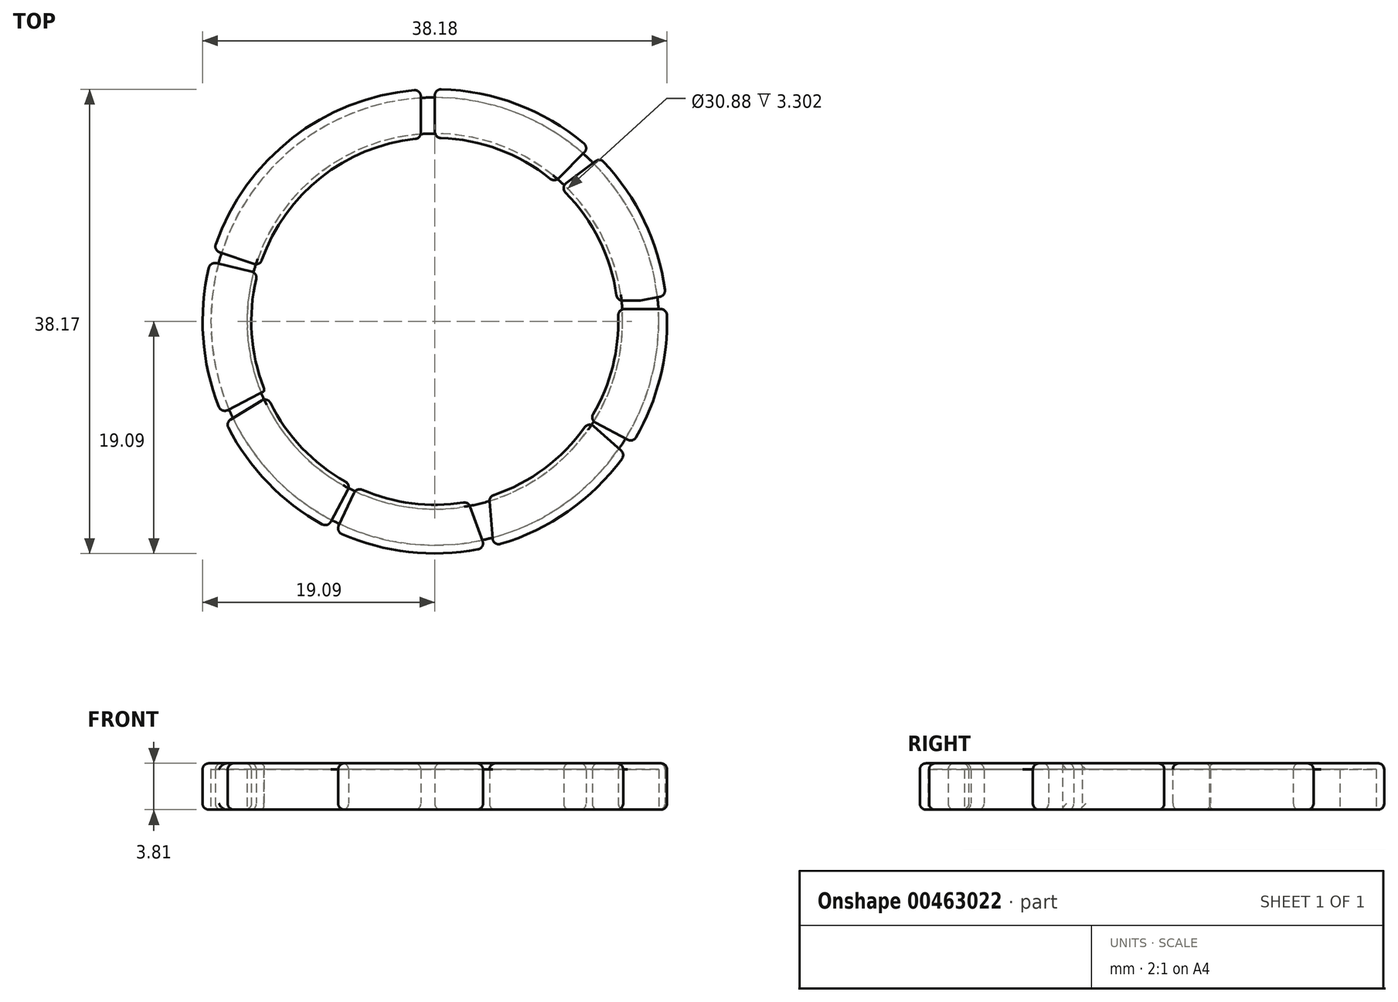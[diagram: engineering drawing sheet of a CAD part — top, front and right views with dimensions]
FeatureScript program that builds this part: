
annotation { "Feature Type Name" : "Feature", "Feature Type Description" : "" }
export const myFeature = defineFeature(function(context is Context, id is Id, definition is map)
    precondition{}
    {
        {
            var Q0;
            Q0=qCreatedBy(makeId("Top.planeOp"),FACE);
            var sketch = newSketch(context, id + "F0", { "sketchPlane" : qUnion([Q0])});
            skCircle(sketch, "E0", {"center": v(0, 0) * mm, "radius": 15.08 * mm});
            skCircle(sketch, "E1", {"center": v(0, 0) * mm, "radius": 19.09 * mm});
            skSolve(sketch);
        }
        {
            var Q0;
            Q0=makeQuery(id+"F0.imprint","IMPRINT",FACE,{"disambiguationData":[TD([[makeQuery(id+"F0.imprint","IMPRINT",EDGE,{"derivedFrom":sQuery(id+"F0.wireOp",EDGE,"E0")}),-1.0]])]});
            extrude(context, id + "F1", {"entities" : qUnion([Q0]), "depth" : 3.8 * mm});
        }
        {
            var Q0;
            Q0=qCreatedBy(makeId("Top.planeOp"),FACE);
            var sketch = newSketch(context, id + "F2", { "sketchPlane" : qUnion([Q0])});
            skLineSegment(sketch, "E2", {"start": v(-1.15, 20.08) * mm, "end": v(-1.15, 14.74) * mm});
            skLineSegment(sketch, "E3", {"start": v(-1.15, 14.74) * mm, "end": v(0, 14.74) * mm});
            skLineSegment(sketch, "E4", {"start": v(0, 14.74) * mm, "end": v(0, 20.5) * mm});
            skLineSegment(sketch, "E5", {"start": v(-1.15, 20.08) * mm, "end": v(0, 20.5) * mm});
            skLineSegment(sketch, "E6", {"start": v(9.54, 11.12) * mm, "end": v(13.13, 14.74) * mm});
            skLineSegment(sketch, "E7", {"start": v(13.13, 14.74) * mm, "end": v(14.06, 13.81) * mm});
            skLineSegment(sketch, "E8", {"start": v(14.06, 13.81) * mm, "end": v(9.54, 10.42) * mm});
            skLineSegment(sketch, "E9", {"start": v(9.54, 10.42) * mm, "end": v(9.54, 11.12) * mm});
            skLineSegment(sketch, "E10", {"start": v(-14.05, 4.45) * mm, "end": v(-18.62, 6) * mm});
            skLineSegment(sketch, "E11", {"start": v(-18.62, 6) * mm, "end": v(-18.62, 4.94) * mm});
            skLineSegment(sketch, "E12", {"start": v(-18.62, 4.94) * mm, "end": v(-14.2, 3.88) * mm});
            skLineSegment(sketch, "E13", {"start": v(-14.2, 3.88) * mm, "end": v(-14.05, 4.45) * mm});
            skLineSegment(sketch, "E14", {"start": v(-17.85, -7.72) * mm, "end": v(-14.05, -5.75) * mm});
            skLineSegment(sketch, "E15", {"start": v(-14.05, -5.75) * mm, "end": v(-13.37, -5.98) * mm});
            skLineSegment(sketch, "E16", {"start": v(-13.37, -5.98) * mm, "end": v(-17.5, -8.5) * mm});
            skLineSegment(sketch, "E17", {"start": v(-17.5, -8.5) * mm, "end": v(-17.85, -7.72) * mm});
            skLineSegment(sketch, "E18", {"start": v(-6.8, -13.21) * mm, "end": v(-8.91, -17.15) * mm});
            skLineSegment(sketch, "E19", {"start": v(-8.91, -17.15) * mm, "end": v(-8.18, -17.4) * mm});
            skLineSegment(sketch, "E20", {"start": v(-8.18, -17.4) * mm, "end": v(-6.31, -13.42) * mm});
            skLineSegment(sketch, "E21", {"start": v(2.55, -14.27) * mm, "end": v(4.38, -19.33) * mm});
            skLineSegment(sketch, "E22", {"start": v(4.38, -19.33) * mm, "end": v(4.89, -19.5) * mm});
            skLineSegment(sketch, "E23", {"start": v(4.89, -19.5) * mm, "end": v(4.38, -13.42) * mm});
            skLineSegment(sketch, "E24", {"start": v(4.38, -13.42) * mm, "end": v(2.55, -14.27) * mm});
            skLineSegment(sketch, "E25", {"start": v(12.05, -7.72) * mm, "end": v(15.85, -11.1) * mm});
            skLineSegment(sketch, "E26", {"start": v(15.85, -11.1) * mm, "end": v(16.67, -10.17) * mm});
            skLineSegment(sketch, "E27", {"start": v(16.67, -10.17) * mm, "end": v(12.05, -7.72) * mm});
            skLineSegment(sketch, "E28", {"start": v(14.16, 1.7) * mm, "end": v(16.83, 1.7) * mm});
            skLineSegment(sketch, "E29", {"start": v(16.83, 1.7) * mm, "end": v(19.72, 2.27) * mm});
            skLineSegment(sketch, "E30", {"start": v(19.72, 2.27) * mm, "end": v(19.96, 1) * mm});
            skLineSegment(sketch, "E31", {"start": v(19.96, 1) * mm, "end": v(14.16, 1) * mm});
            skLineSegment(sketch, "E32", {"start": v(14.16, 1) * mm, "end": v(14.16, 1.7) * mm});
            skLineSegment(sketch, "E33", {"start": v(-6.31, -13.42) * mm, "end": v(-6.8, -13.21) * mm});
            skSolve(sketch);
        }
        {
            var Q0;
            Q0 = qSketchRegion(id + "F2", true);
            extrude(context, id + "F3", {"entities" : qUnion([Q0]), "operationType" : NewBodyOperationType.REMOVE, "oppositeDirection" : true, "depth" : -25.4 * mm});
        }
        {
            var Q0;
            {var subQ0=sQuery(id+"F0.wireOp",EDGE,"E1");Q0=makeQuery(id+"F3.boolean.opBoolean","SPLIT",EDGE,{"disambiguationData":[TD([makeQuery(id+"F3.opExtrude","SWEPT_FACE",FACE,{"disambiguationData":[OSD([sQuery(id+"F2.wireOp",EDGE,"E4")])]})])],"derivedFrom":makeQuery(id+"F1.opExtrude","CAP_EDGE",EDGE,{"disambiguationData":[OSD([subQ0])],"isStart":false})});}
            var Q1;
            {var subQ0=sQuery(id+"F0.wireOp",EDGE,"E1");Q1=makeQuery(id+"F3.boolean.opBoolean","SPLIT",FACE,{"disambiguationData":[TD([makeQuery(id+"F3.opExtrude","SWEPT_FACE",FACE,{"disambiguationData":[OSD([sQuery(id+"F2.wireOp",EDGE,"E4")])]})])],"derivedFrom":makeQuery(id+"F1.opExtrude","SWEPT_FACE",FACE,{"disambiguationData":[OSD([subQ0])]})});}
            var Q2;
            {var subQ0=sQuery(id+"F0.wireOp",EDGE,"E0");var subQ1=sQuery(id+"F0.wireOp",EDGE,"E1");Q2=makeQuery(id+"F3.boolean.opBoolean","SPLIT",FACE,{"disambiguationData":[TD([makeQuery(id+"F3.opExtrude","SWEPT_FACE",FACE,{"disambiguationData":[OSD([sQuery(id+"F2.wireOp",EDGE,"E4")])]})])],"derivedFrom":makeQuery(id+"F1.opExtrude","CAP_FACE",FACE,{"disambiguationData":[OSD([subQ0,subQ1])],"isStart":true})});}
            var Q3;
            {var subQ0=sQuery(id+"F0.wireOp",EDGE,"E1");Q3=makeQuery(id+"F3.boolean.opBoolean","SPLIT",EDGE,{"disambiguationData":[TD([makeQuery(id+"F3.opExtrude","SWEPT_FACE",FACE,{"disambiguationData":[OSD([sQuery(id+"F2.wireOp",EDGE,"E4")])]})])],"derivedFrom":makeQuery(id+"F1.opExtrude","CAP_EDGE",EDGE,{"disambiguationData":[OSD([subQ0])],"isStart":true})});}
            var Q4;
            {var subQ0=sQuery(id+"F0.wireOp",EDGE,"E0");Q4=makeQuery(id+"F3.boolean.opBoolean","SPLIT",EDGE,{"disambiguationData":[TD([makeQuery(id+"F3.opExtrude","SWEPT_FACE",FACE,{"disambiguationData":[OSD([sQuery(id+"F2.wireOp",EDGE,"E4")])]})])],"derivedFrom":makeQuery(id+"F1.opExtrude","CAP_EDGE",EDGE,{"disambiguationData":[OSD([subQ0])],"isStart":false})});}
            var Q5;
            {var subQ0=sQuery(id+"F0.wireOp",EDGE,"E0");Q5=makeQuery(id+"F3.boolean.opBoolean","SPLIT",EDGE,{"disambiguationData":[TD([makeQuery(id+"F3.opExtrude","SWEPT_FACE",FACE,{"disambiguationData":[OSD([sQuery(id+"F2.wireOp",EDGE,"E4")])]})])],"derivedFrom":makeQuery(id+"F1.opExtrude","CAP_EDGE",EDGE,{"disambiguationData":[OSD([subQ0])],"isStart":true})});}
            var Q6;
            {var subQ1=sQuery(id+"F0.wireOp",EDGE,"E0");Q6=makeQuery(id+"F3.boolean.opBoolean","SPLIT",FACE,{"disambiguationData":[TD([makeQuery(id+"F3.opExtrude","SWEPT_FACE",FACE,{"disambiguationData":[OSD([sQuery(id+"F2.wireOp",EDGE,"E4")])]})])],"derivedFrom":makeQuery(id+"F1.opExtrude","SWEPT_FACE",FACE,{"disambiguationData":[OSD([subQ1])]})});}
            var Q7;
            Q7=makeQuery(id+"F3.boolean.opBoolean","COPY",FACE,{"derivedFrom":makeQuery(id+"F3.opExtrude","SWEPT_FACE",FACE,{"disambiguationData":[OSD([sQuery(id+"F2.wireOp",EDGE,"E6")])]})});
            var Q8;
            Q8=makeQuery(id+"F3.boolean.opBoolean","COPY",FACE,{"derivedFrom":makeQuery(id+"F3.opExtrude","SWEPT_FACE",FACE,{"disambiguationData":[OSD([sQuery(id+"F2.wireOp",EDGE,"E4")])]})});
            var Q9;
            {var subQ0=sQuery(id+"F0.wireOp",EDGE,"E0");var subQ1=sQuery(id+"F0.wireOp",EDGE,"E1");Q9=makeQuery(id+"F3.boolean.opBoolean","SPLIT",FACE,{"disambiguationData":[TD([makeQuery(id+"F3.opExtrude","SWEPT_FACE",FACE,{"disambiguationData":[OSD([sQuery(id+"F2.wireOp",EDGE,"E2")])]})])],"derivedFrom":makeQuery(id+"F1.opExtrude","CAP_FACE",FACE,{"disambiguationData":[OSD([subQ0,subQ1])],"isStart":false})});}
            var Q10;
            {var subQ1=sQuery(id+"F0.wireOp",EDGE,"E0");Q10=makeQuery(id+"F3.boolean.opBoolean","SPLIT",FACE,{"disambiguationData":[TD([makeQuery(id+"F3.opExtrude","SWEPT_FACE",FACE,{"disambiguationData":[OSD([sQuery(id+"F2.wireOp",EDGE,"E2")])]})])],"derivedFrom":makeQuery(id+"F1.opExtrude","SWEPT_FACE",FACE,{"disambiguationData":[OSD([subQ1])]})});}
            var Q11;
            Q11=makeQuery(id+"F3.boolean.opBoolean","COPY",FACE,{"derivedFrom":makeQuery(id+"F3.opExtrude","SWEPT_FACE",FACE,{"disambiguationData":[OSD([sQuery(id+"F2.wireOp",EDGE,"E2")])]})});
            var Q12;
            Q12=makeQuery(id+"F3.boolean.opBoolean","COPY",FACE,{"derivedFrom":makeQuery(id+"F3.opExtrude","SWEPT_FACE",FACE,{"disambiguationData":[OSD([sQuery(id+"F2.wireOp",EDGE,"E10")])]})});
            var Q13;
            Q13=makeQuery(id+"F3.boolean.opBoolean","COPY",FACE,{"derivedFrom":makeQuery(id+"F3.opExtrude","SWEPT_FACE",FACE,{"disambiguationData":[OSD([sQuery(id+"F2.wireOp",EDGE,"E29")])]})});
            var Q14;
            Q14=makeQuery(id+"F3.boolean.opBoolean","INTERSECT",EDGE,{"derivedFrom":[makeQuery(id+"F1.opExtrude","CAP_FACE",FACE,{"disambiguationData":[OSD([sQuery(id+"F0.wireOp",EDGE,"E0"),sQuery(id+"F0.wireOp",EDGE,"E1")])],"isStart":false}),makeQuery(id+"F3.opExtrude","SWEPT_FACE",FACE,{"disambiguationData":[OSD([sQuery(id+"F2.wireOp",EDGE,"E28")])]})]});
            var Q15;
            {var subQ0=sQuery(id+"F0.wireOp",EDGE,"E0");var subQ1=sQuery(id+"F0.wireOp",EDGE,"E1");Q15=makeQuery(id+"F3.boolean.opBoolean","SPLIT",FACE,{"disambiguationData":[TD([makeQuery(id+"F3.opExtrude","SWEPT_FACE",FACE,{"disambiguationData":[OSD([sQuery(id+"F2.wireOp",EDGE,"E8")])]})])],"derivedFrom":makeQuery(id+"F1.opExtrude","CAP_FACE",FACE,{"disambiguationData":[OSD([subQ0,subQ1])],"isStart":false})});}
            var Q16;
            {var subQ0=sQuery(id+"F0.wireOp",EDGE,"E1");Q16=makeQuery(id+"F3.boolean.opBoolean","SPLIT",FACE,{"disambiguationData":[TD([makeQuery(id+"F3.opExtrude","SWEPT_FACE",FACE,{"disambiguationData":[OSD([sQuery(id+"F2.wireOp",EDGE,"E8")])]})])],"derivedFrom":makeQuery(id+"F1.opExtrude","SWEPT_FACE",FACE,{"disambiguationData":[OSD([subQ0])]})});}
            var Q17;
            {var subQ1=sQuery(id+"F0.wireOp",EDGE,"E0");Q17=makeQuery(id+"F3.boolean.opBoolean","SPLIT",FACE,{"disambiguationData":[TD([makeQuery(id+"F3.opExtrude","SWEPT_FACE",FACE,{"disambiguationData":[OSD([sQuery(id+"F2.wireOp",EDGE,"E8")])]})])],"derivedFrom":makeQuery(id+"F1.opExtrude","SWEPT_FACE",FACE,{"disambiguationData":[OSD([subQ1])]})});}
            var Q18;
            {var subQ0=sQuery(id+"F0.wireOp",EDGE,"E1");Q18=makeQuery(id+"F3.boolean.opBoolean","SPLIT",FACE,{"disambiguationData":[TD([makeQuery(id+"F3.opExtrude","SWEPT_FACE",FACE,{"disambiguationData":[OSD([sQuery(id+"F2.wireOp",EDGE,"E2")])]})])],"derivedFrom":makeQuery(id+"F1.opExtrude","SWEPT_FACE",FACE,{"disambiguationData":[OSD([subQ0])]})});}
            var Q19;
            {var subQ0=sQuery(id+"F0.wireOp",EDGE,"E0");var subQ1=sQuery(id+"F0.wireOp",EDGE,"E1");Q19=makeQuery(id+"F3.boolean.opBoolean","SPLIT",FACE,{"disambiguationData":[TD([makeQuery(id+"F3.opExtrude","SWEPT_FACE",FACE,{"disambiguationData":[OSD([sQuery(id+"F2.wireOp",EDGE,"E27")])]})])],"derivedFrom":makeQuery(id+"F1.opExtrude","CAP_FACE",FACE,{"disambiguationData":[OSD([subQ0,subQ1])],"isStart":false})});}
            var Q20;
            {var subQ0=sQuery(id+"F0.wireOp",EDGE,"E1");Q20=makeQuery(id+"F3.boolean.opBoolean","SPLIT",FACE,{"disambiguationData":[TD([makeQuery(id+"F3.opExtrude","SWEPT_FACE",FACE,{"disambiguationData":[OSD([sQuery(id+"F2.wireOp",EDGE,"E27")])]})])],"derivedFrom":makeQuery(id+"F1.opExtrude","SWEPT_FACE",FACE,{"disambiguationData":[OSD([subQ0])]})});}
            var Q21;
            {var subQ0=sQuery(id+"F0.wireOp",EDGE,"E0");var subQ1=sQuery(id+"F0.wireOp",EDGE,"E1");Q21=makeQuery(id+"F3.boolean.opBoolean","SPLIT",FACE,{"disambiguationData":[TD([makeQuery(id+"F3.opExtrude","SWEPT_FACE",FACE,{"disambiguationData":[OSD([sQuery(id+"F2.wireOp",EDGE,"E27")])]})])],"derivedFrom":makeQuery(id+"F1.opExtrude","CAP_FACE",FACE,{"disambiguationData":[OSD([subQ0,subQ1])],"isStart":true})});}
            var Q22;
            {var subQ0=sQuery(id+"F0.wireOp",EDGE,"E0");var subQ1=sQuery(id+"F0.wireOp",EDGE,"E1");Q22=makeQuery(id+"F3.boolean.opBoolean","SPLIT",FACE,{"disambiguationData":[TD([makeQuery(id+"F3.opExtrude","SWEPT_FACE",FACE,{"disambiguationData":[OSD([sQuery(id+"F2.wireOp",EDGE,"E23")])]})])],"derivedFrom":makeQuery(id+"F1.opExtrude","CAP_FACE",FACE,{"disambiguationData":[OSD([subQ0,subQ1])],"isStart":true})});}
            var Q23;
            {var subQ0=sQuery(id+"F0.wireOp",EDGE,"E1");Q23=makeQuery(id+"F3.boolean.opBoolean","SPLIT",FACE,{"disambiguationData":[TD([makeQuery(id+"F3.opExtrude","SWEPT_FACE",FACE,{"disambiguationData":[OSD([sQuery(id+"F2.wireOp",EDGE,"E23")])]})])],"derivedFrom":makeQuery(id+"F1.opExtrude","SWEPT_FACE",FACE,{"disambiguationData":[OSD([subQ0])]})});}
            var Q24;
            {var subQ0=sQuery(id+"F0.wireOp",EDGE,"E0");var subQ1=sQuery(id+"F0.wireOp",EDGE,"E1");Q24=makeQuery(id+"F3.boolean.opBoolean","SPLIT",FACE,{"disambiguationData":[TD([makeQuery(id+"F3.opExtrude","SWEPT_FACE",FACE,{"disambiguationData":[OSD([sQuery(id+"F2.wireOp",EDGE,"E23")])]})])],"derivedFrom":makeQuery(id+"F1.opExtrude","CAP_FACE",FACE,{"disambiguationData":[OSD([subQ0,subQ1])],"isStart":false})});}
            var Q25;
            {var subQ0=sQuery(id+"F0.wireOp",EDGE,"E0");var subQ1=sQuery(id+"F0.wireOp",EDGE,"E1");Q25=makeQuery(id+"F3.boolean.opBoolean","SPLIT",FACE,{"disambiguationData":[TD([makeQuery(id+"F3.opExtrude","SWEPT_FACE",FACE,{"disambiguationData":[OSD([sQuery(id+"F2.wireOp",EDGE,"E20")])]})])],"derivedFrom":makeQuery(id+"F1.opExtrude","CAP_FACE",FACE,{"disambiguationData":[OSD([subQ0,subQ1])],"isStart":false})});}
            var Q26;
            {var subQ0=sQuery(id+"F0.wireOp",EDGE,"E1");Q26=makeQuery(id+"F3.boolean.opBoolean","SPLIT",FACE,{"disambiguationData":[TD([makeQuery(id+"F3.opExtrude","SWEPT_FACE",FACE,{"disambiguationData":[OSD([sQuery(id+"F2.wireOp",EDGE,"E20")])]})])],"derivedFrom":makeQuery(id+"F1.opExtrude","SWEPT_FACE",FACE,{"disambiguationData":[OSD([subQ0])]})});}
            var Q27;
            {var subQ0=sQuery(id+"F0.wireOp",EDGE,"E0");var subQ1=sQuery(id+"F0.wireOp",EDGE,"E1");Q27=makeQuery(id+"F3.boolean.opBoolean","SPLIT",FACE,{"disambiguationData":[TD([makeQuery(id+"F3.opExtrude","SWEPT_FACE",FACE,{"disambiguationData":[OSD([sQuery(id+"F2.wireOp",EDGE,"E20")])]})])],"derivedFrom":makeQuery(id+"F1.opExtrude","CAP_FACE",FACE,{"disambiguationData":[OSD([subQ0,subQ1])],"isStart":true})});}
            var Q28;
            {var subQ0=sQuery(id+"F0.wireOp",EDGE,"E0");var subQ1=sQuery(id+"F0.wireOp",EDGE,"E1");Q28=makeQuery(id+"F3.boolean.opBoolean","SPLIT",FACE,{"disambiguationData":[TD([makeQuery(id+"F3.opExtrude","SWEPT_FACE",FACE,{"disambiguationData":[OSD([sQuery(id+"F2.wireOp",EDGE,"E16")])]})])],"derivedFrom":makeQuery(id+"F1.opExtrude","CAP_FACE",FACE,{"disambiguationData":[OSD([subQ0,subQ1])],"isStart":true})});}
            var Q29;
            {var subQ0=sQuery(id+"F0.wireOp",EDGE,"E1");Q29=makeQuery(id+"F3.boolean.opBoolean","SPLIT",FACE,{"disambiguationData":[TD([makeQuery(id+"F3.opExtrude","SWEPT_FACE",FACE,{"disambiguationData":[OSD([sQuery(id+"F2.wireOp",EDGE,"E16")])]})])],"derivedFrom":makeQuery(id+"F1.opExtrude","SWEPT_FACE",FACE,{"disambiguationData":[OSD([subQ0])]})});}
            var Q30;
            {var subQ0=sQuery(id+"F0.wireOp",EDGE,"E0");var subQ1=sQuery(id+"F0.wireOp",EDGE,"E1");Q30=makeQuery(id+"F3.boolean.opBoolean","SPLIT",FACE,{"disambiguationData":[TD([makeQuery(id+"F3.opExtrude","SWEPT_FACE",FACE,{"disambiguationData":[OSD([sQuery(id+"F2.wireOp",EDGE,"E16")])]})])],"derivedFrom":makeQuery(id+"F1.opExtrude","CAP_FACE",FACE,{"disambiguationData":[OSD([subQ0,subQ1])],"isStart":false})});}
            var Q31;
            {var subQ0=sQuery(id+"F0.wireOp",EDGE,"E1");Q31=makeQuery(id+"F3.boolean.opBoolean","SPLIT",FACE,{"disambiguationData":[TD([makeQuery(id+"F3.opExtrude","SWEPT_FACE",FACE,{"disambiguationData":[OSD([sQuery(id+"F2.wireOp",EDGE,"E12")])]})])],"derivedFrom":makeQuery(id+"F1.opExtrude","SWEPT_FACE",FACE,{"disambiguationData":[OSD([subQ0])]})});}
            var Q32;
            Q32=makeQuery(id+"F3.boolean.opBoolean","COPY",FACE,{"derivedFrom":makeQuery(id+"F3.opExtrude","SWEPT_FACE",FACE,{"disambiguationData":[OSD([sQuery(id+"F2.wireOp",EDGE,"E12")])]})});
            var Q33;
            {var subQ1=sQuery(id+"F0.wireOp",EDGE,"E0");Q33=makeQuery(id+"F3.boolean.opBoolean","SPLIT",FACE,{"disambiguationData":[TD([makeQuery(id+"F3.opExtrude","SWEPT_FACE",FACE,{"disambiguationData":[OSD([sQuery(id+"F2.wireOp",EDGE,"E12")])]})])],"derivedFrom":makeQuery(id+"F1.opExtrude","SWEPT_FACE",FACE,{"disambiguationData":[OSD([subQ1])]})});}
            var Q34;
            {var subQ1=sQuery(id+"F0.wireOp",EDGE,"E0");Q34=makeQuery(id+"F3.boolean.opBoolean","SPLIT",FACE,{"disambiguationData":[TD([makeQuery(id+"F3.opExtrude","SWEPT_FACE",FACE,{"disambiguationData":[OSD([sQuery(id+"F2.wireOp",EDGE,"E27")])]})])],"derivedFrom":makeQuery(id+"F1.opExtrude","SWEPT_FACE",FACE,{"disambiguationData":[OSD([subQ1])]})});}
            var Q35;
            {var subQ1=sQuery(id+"F0.wireOp",EDGE,"E0");Q35=makeQuery(id+"F3.boolean.opBoolean","SPLIT",FACE,{"disambiguationData":[TD([makeQuery(id+"F3.opExtrude","SWEPT_FACE",FACE,{"disambiguationData":[OSD([sQuery(id+"F2.wireOp",EDGE,"E23")])]})])],"derivedFrom":makeQuery(id+"F1.opExtrude","SWEPT_FACE",FACE,{"disambiguationData":[OSD([subQ1])]})});}
            var Q36;
            {var subQ1=sQuery(id+"F0.wireOp",EDGE,"E0");Q36=makeQuery(id+"F3.boolean.opBoolean","SPLIT",FACE,{"disambiguationData":[TD([makeQuery(id+"F3.opExtrude","SWEPT_FACE",FACE,{"disambiguationData":[OSD([sQuery(id+"F2.wireOp",EDGE,"E20")])]})])],"derivedFrom":makeQuery(id+"F1.opExtrude","SWEPT_FACE",FACE,{"disambiguationData":[OSD([subQ1])]})});}
            var Q37;
            {var subQ1=sQuery(id+"F0.wireOp",EDGE,"E0");Q37=makeQuery(id+"F3.boolean.opBoolean","SPLIT",FACE,{"disambiguationData":[TD([makeQuery(id+"F3.opExtrude","SWEPT_FACE",FACE,{"disambiguationData":[OSD([sQuery(id+"F2.wireOp",EDGE,"E16")])]})])],"derivedFrom":makeQuery(id+"F1.opExtrude","SWEPT_FACE",FACE,{"disambiguationData":[OSD([subQ1])]})});}
            var Q38;
            {var subQ0=sQuery(id+"F0.wireOp",EDGE,"E0");var subQ1=sQuery(id+"F0.wireOp",EDGE,"E1");Q38=makeQuery(id+"F3.boolean.opBoolean","SPLIT",FACE,{"disambiguationData":[TD([makeQuery(id+"F3.opExtrude","SWEPT_FACE",FACE,{"disambiguationData":[OSD([sQuery(id+"F2.wireOp",EDGE,"E8")])]})])],"derivedFrom":makeQuery(id+"F1.opExtrude","CAP_FACE",FACE,{"disambiguationData":[OSD([subQ0,subQ1])],"isStart":true})});}
            fillet(context, id + "F4", {"entities" : qUnion([Q0, Q1, Q2, Q3, Q4, Q5, Q6, Q7, Q8, Q9, Q10, Q11, Q12, Q13, Q14, Q15, Q16, Q17, Q18, Q19, Q20, Q21, Q22, Q23, Q24, Q25, Q26, Q27, Q28, Q29, Q30, Q31, Q32, Q33, Q34, Q35, Q36, Q37, Q38]), "radius" : 0.5 * mm, "tangentPropagation" : true, "allowEdgeOverflow" : false});
        }
        {
            var Q0;
            Q0=qCreatedBy(makeId("Top.planeOp"),FACE);
            var sketch = newSketch(context, id + "F5", { "sketchPlane" : qUnion([Q0])});
            skCircle(sketch, "E34", {"center": v(0, 0) * mm, "radius": 18.4 * mm});
            skCircle(sketch, "E35", {"center": v(0, 0) * mm, "radius": 15.44 * mm});
            skSolve(sketch);
        }
        {
            var Q0;
            Q0=makeQuery(id+"F5.imprint","IMPRINT",FACE,{"disambiguationData":[TD([[makeQuery(id+"F5.imprint","IMPRINT",EDGE,{"derivedFrom":sQuery(id+"F5.wireOp",EDGE,"E34")}),1.0]])]});
            extrude(context, id + "F6", {"entities" : qUnion([Q0]), "depth" : 3.3 * mm});
        }
    });
